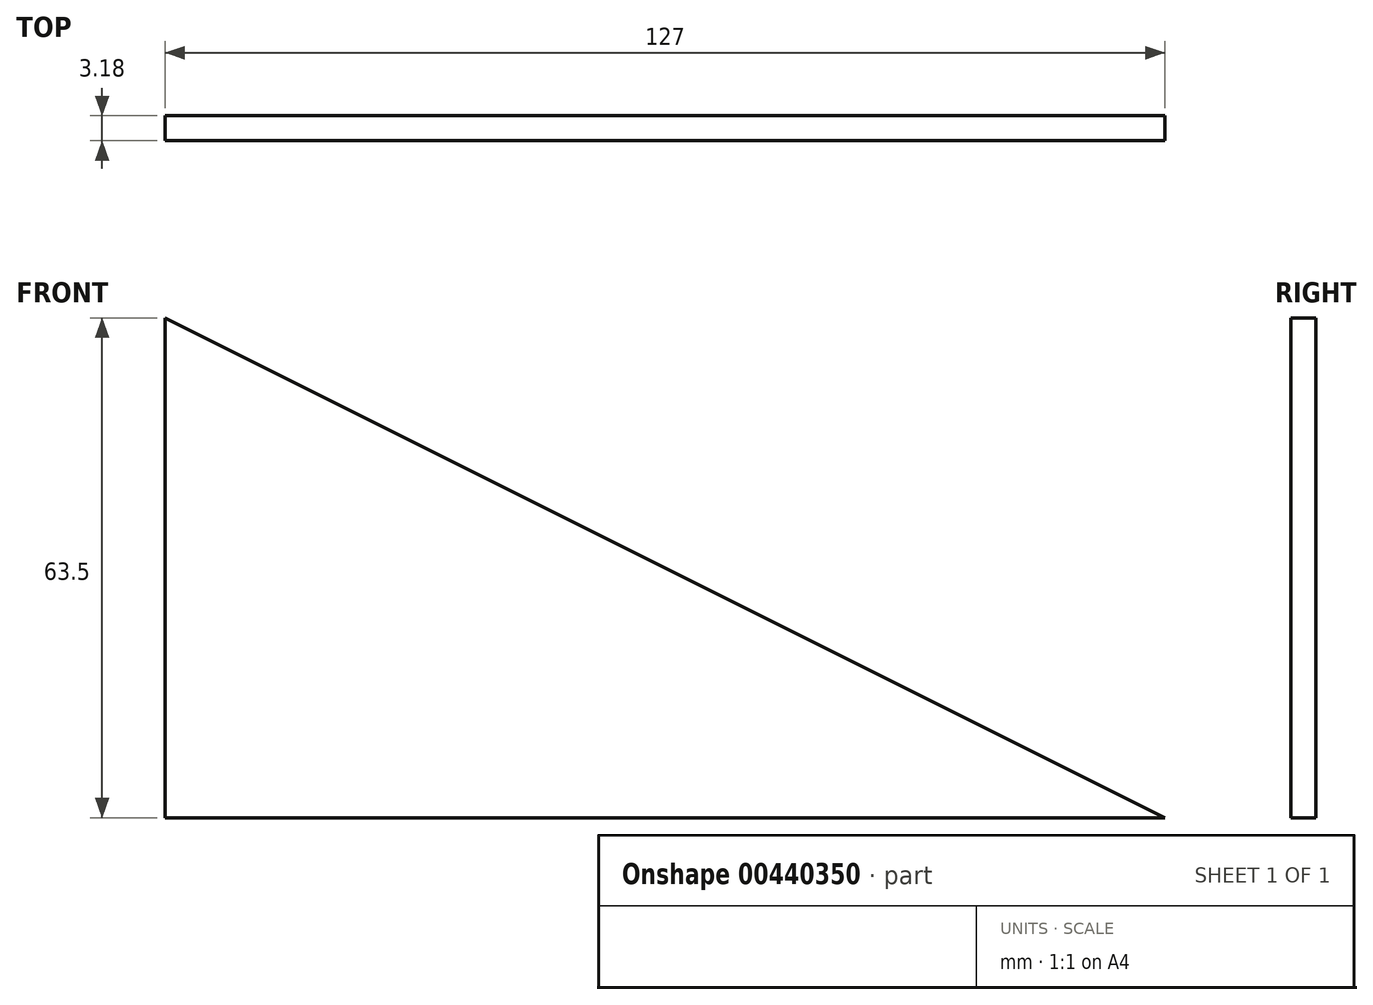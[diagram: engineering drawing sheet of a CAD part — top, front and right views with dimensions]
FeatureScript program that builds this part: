
annotation { "Feature Type Name" : "Feature", "Feature Type Description" : "" }
export const myFeature = defineFeature(function(context is Context, id is Id, definition is map)
    precondition{}
    {
        {
            var Q0;
            Q0=qCreatedBy(makeId("Front.planeOp"),FACE);
            var sketch = newSketch(context, id + "F0", { "sketchPlane" : qUnion([Q0])});
            skLineSegment(sketch, "E0.bottom", {"start": v(-63.5, 31.75) * mm, "end": v(63.5, 31.75) * mm});
            skLineSegment(sketch, "E0.top", {"start": v(-63.5, -31.75) * mm, "end": v(63.5, -31.75) * mm});
            skLineSegment(sketch, "E0.left", {"start": v(-63.5, 31.75) * mm, "end": v(-63.5, -31.75) * mm});
            skLineSegment(sketch, "E0.right", {"start": v(63.5, 31.75) * mm, "end": v(63.5, -31.75) * mm});
            skPoint(sketch, "E0.middle", {"position": v(0, 0) * mm});
            skLineSegment(sketch, "E1", {"start": v(-63.5, 31.75) * mm, "end": v(63.5, -31.75) * mm});
            skSolve(sketch);
        }
        {
            var Q0;
            Q0=makeQuery(id+"F0.imprint","IMPRINT",FACE,{"disambiguationData":[TD([[makeQuery(id+"F0.imprint","IMPRINT",EDGE,{"derivedFrom":sQuery(id+"F0.wireOp",EDGE,"E0.top")}),1.0]])]});
            extrude(context, id + "F1", {"entities" : qUnion([Q0]), "endBound" : BoundingType.SYMMETRIC, "depth" : 3.17 * mm});
        }
    });
